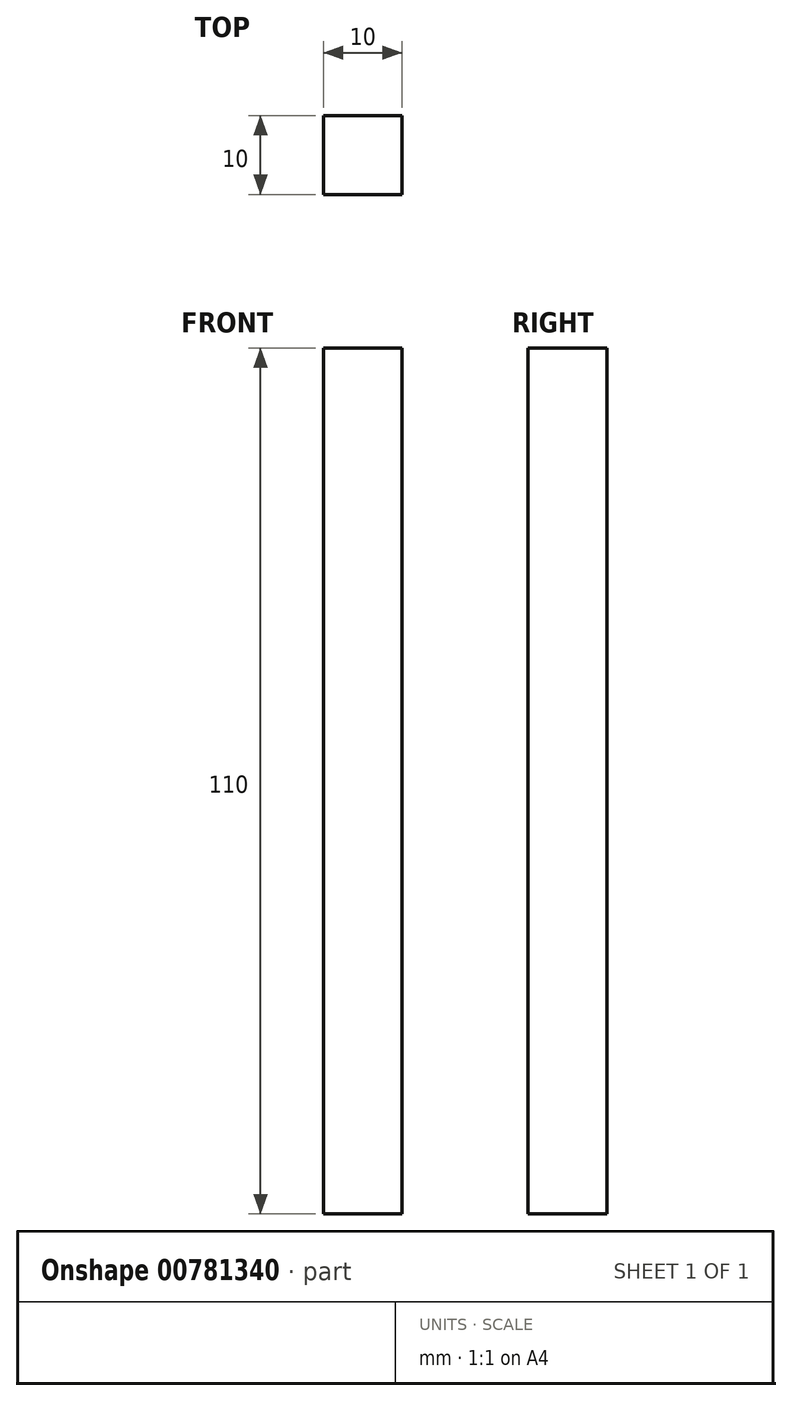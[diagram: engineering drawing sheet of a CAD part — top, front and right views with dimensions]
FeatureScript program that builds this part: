
annotation { "Feature Type Name" : "Feature", "Feature Type Description" : "" }
export const myFeature = defineFeature(function(context is Context, id is Id, definition is map)
    precondition{}
    {
        {
            var Q0;
            Q0=qCreatedBy(makeId("Top.planeOp"),FACE);
            var sketch = newSketch(context, id + "F0", { "sketchPlane" : qUnion([Q0])});
            skLineSegment(sketch, "E0.bottom", {"start": v(5, -5) * mm, "end": v(-5, -5) * mm});
            skLineSegment(sketch, "E0.top", {"start": v(5, 5) * mm, "end": v(-5, 5) * mm});
            skLineSegment(sketch, "E0.left", {"start": v(5, -5) * mm, "end": v(5, 5) * mm});
            skLineSegment(sketch, "E0.right", {"start": v(-5, -5) * mm, "end": v(-5, 5) * mm});
            skPoint(sketch, "E0.middle", {"position": v(0, 0) * mm});
            skSolve(sketch);
        }
        {
            var Q0;
            Q0 = qSketchRegion(id + "F0", true);
            extrude(context, id + "F1", {"entities" : qUnion([Q0]), "endBound" : BoundingType.SYMMETRIC, "depth" : 110 * mm, "offsetDistance" : 25 * mm});
        }
    });
